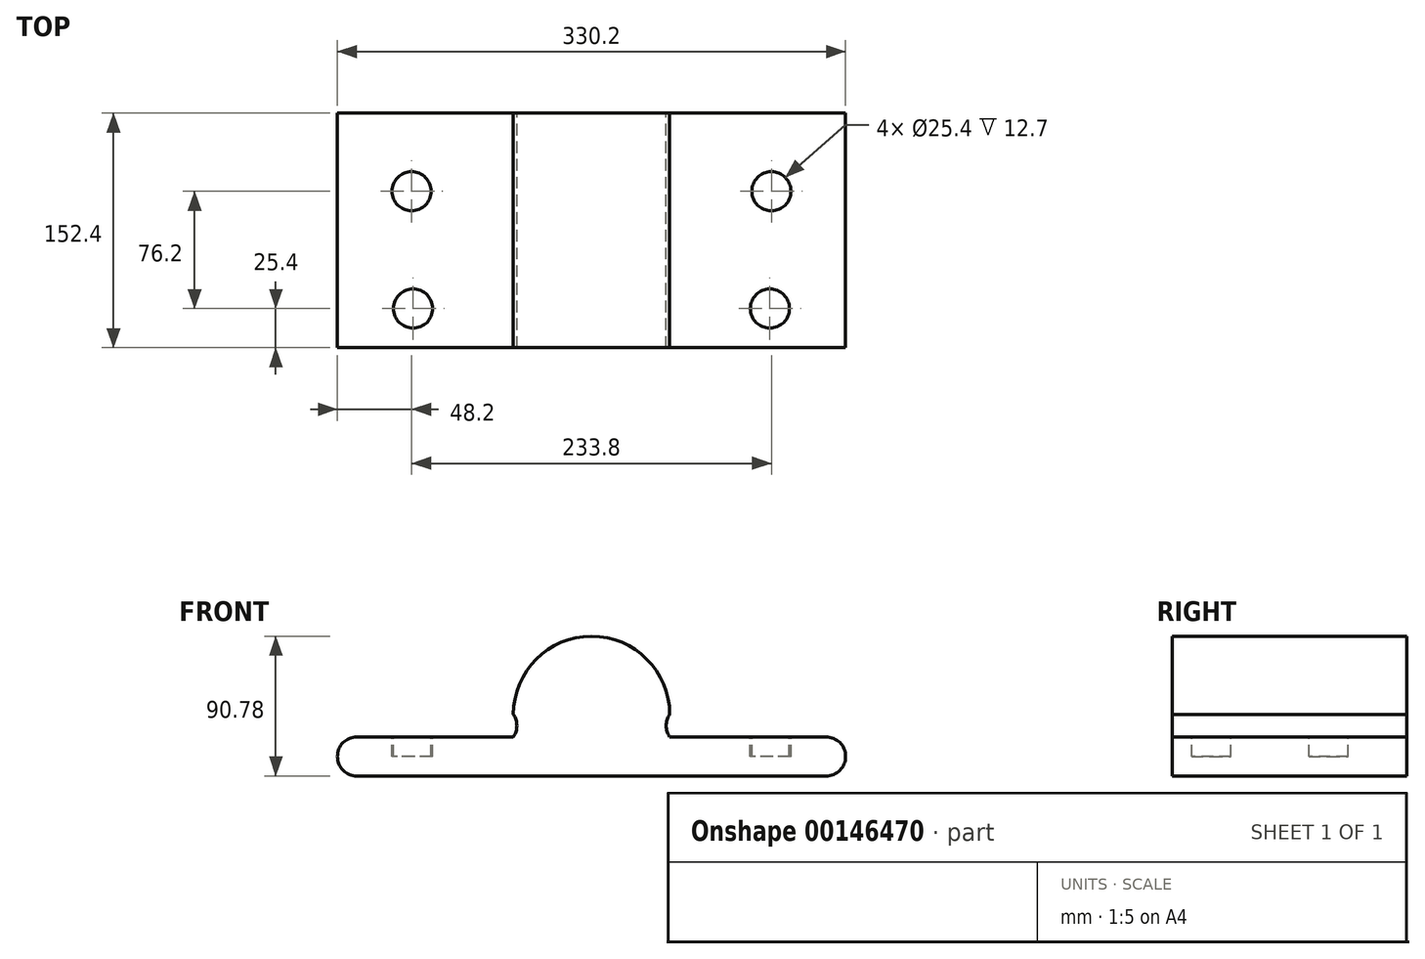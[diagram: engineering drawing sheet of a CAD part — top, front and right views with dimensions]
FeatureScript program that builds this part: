
annotation { "Feature Type Name" : "Feature", "Feature Type Description" : "" }
export const myFeature = defineFeature(function(context is Context, id is Id, definition is map)
    precondition{}
    {
        {
            var Q0;
            Q0=qCreatedBy(makeId("Front.planeOp"),FACE);
            var sketch = newSketch(context, id + "F0", { "sketchPlane" : qUnion([Q0])});
            skLineSegment(sketch, "E0", {"start": v(-152.4, -39.98) * mm, "end": v(152.4, -39.98) * mm});
            skArc(sketch, "E1", {"start": v(50.8, 0) * mm, "mid": v(0, 50.8) * mm, "end": v(-50.8, 0) * mm});
            skCircle(sketch, "E2", {"center": v(0, 0) * mm, "radius": 25.4 * mm});
            skLineSegment(sketch, "E3", {"start": v(25.4, 0) * mm, "end": v(50.8, 0) * mm});
            skArc(sketch, "E4", {"start": v(50.8, 0) * mm, "mid": v(48.5, -7.29) * mm, "end": v(50.8, -14.58) * mm});
            skLineSegment(sketch, "E5", {"start": v(50.8, -14.58) * mm, "end": v(152.4, -14.58) * mm});
            skArc(sketch, "E6.MirrorCS", {"start": v(-50.8, 0) * mm, "mid": v(-48.5, -7.29) * mm, "end": v(-50.8, -14.58) * mm});
            skLineSegment(sketch, "E7.MirrorCS", {"start": v(-50.8, -14.58) * mm, "end": v(-152.4, -14.58) * mm});
            skArc(sketch, "E8", {"start": v(-152.4, -14.58) * mm, "mid": v(-165.1, -27.28) * mm, "end": v(-152.4, -39.98) * mm});
            skArc(sketch, "E9.MirrorCS", {"start": v(152.4, -14.58) * mm, "mid": v(165.1, -27.28) * mm, "end": v(152.4, -39.98) * mm});
            skSolve(sketch);
        }
        {
            var Q0;
            Q0=makeQuery(id+"F0.imprint","IMPRINT",FACE,{"disambiguationData":[TD([[makeQuery(id+"F0.imprint","IMPRINT",EDGE,{"derivedFrom":sQuery(id+"F0.wireOp",EDGE,"E0")}),1.0]])]});
            var Q1;
            Q1=makeQuery(id+"F0.imprint","IMPRINT",FACE,{"disambiguationData":[TD([[makeQuery(id+"F0.imprint","IMPRINT",EDGE,{"derivedFrom":sQuery(id+"F0.wireOp",EDGE,"E2")}),1.0]])]});
            extrude(context, id + "F1", {"entities" : qUnion([Q0, Q1]), "depth" : 152.4 * mm});
        }
        {
            var Q0;
            Q0=makeQuery(id+"F1.opExtrude","SWEPT_FACE",FACE,{"disambiguationData":[OSD([sQuery(id+"F0.wireOp",EDGE,"E7.MirrorCS")])]});
            var sketch = newSketch(context, id + "F2", { "sketchPlane" : qUnion([Q0])});
            skCircle(sketch, "E10", {"center": v(115.91, -127) * mm, "radius": 12.7 * mm});
            skCircle(sketch, "E11", {"center": v(116.9, -50.8) * mm, "radius": 12.7 * mm});
            skCircle(sketch, "E12.MirrorC", {"center": v(-115.91, -127) * mm, "radius": 12.7 * mm});
            skCircle(sketch, "E13.MirrorC", {"center": v(-116.9, -50.8) * mm, "radius": 12.7 * mm});
            skSolve(sketch);
        }
        {
            var Q0;
            Q0 = qSketchRegion(id + "F2", true);
            var Q1;
            Q1=makeQuery(id+"F1.opExtrude","SWEPT_FACE",FACE,{"disambiguationData":[OSD([sQuery(id+"F0.wireOp",EDGE,"E0")])]});
            extrude(context, id + "F3", {"entities" : qUnion([Q0, Q1]), "operationType" : NewBodyOperationType.REMOVE, "oppositeDirection" : true, "depth" : 12.7 * mm});
        }
    });
